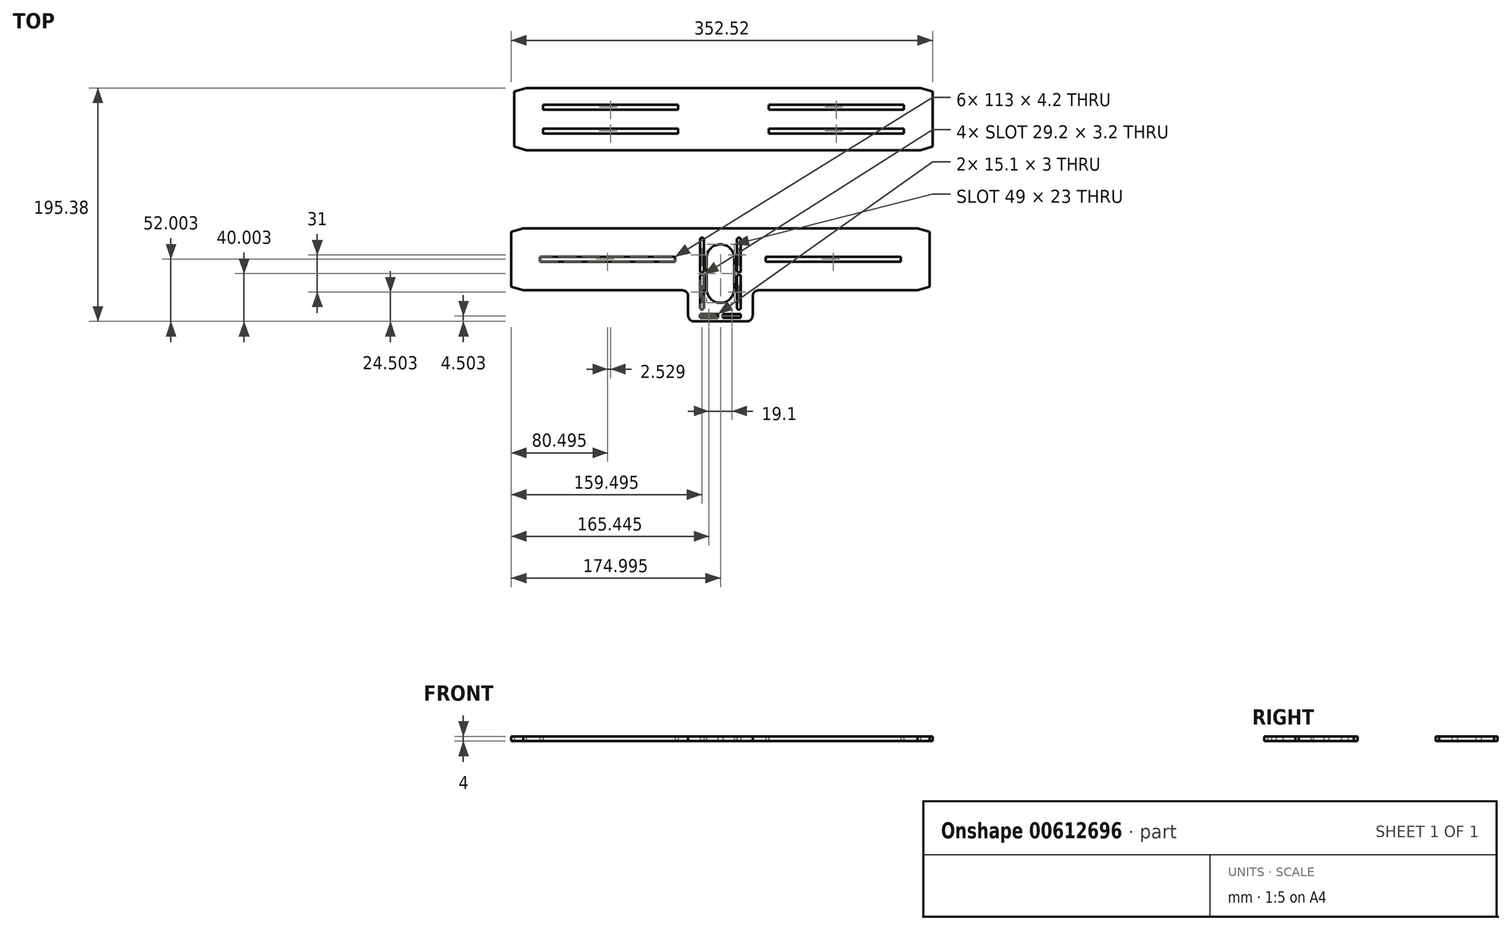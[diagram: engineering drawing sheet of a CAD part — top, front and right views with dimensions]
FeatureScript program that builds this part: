
annotation { "Feature Type Name" : "Feature", "Feature Type Description" : "" }
export const myFeature = defineFeature(function(context is Context, id is Id, definition is map)
    precondition{}
    {
        {
            var Q0;
            Q0=qCreatedBy(makeId("Top.planeOp"),FACE);
            var sketch = newSketch(context, id + "F0", { "sketchPlane" : qUnion([Q0])});
            skLineSegment(sketch, "E0", {"start": v(-166.26, -19.69) * mm, "end": v(-176.26, -22.69) * mm});
            skLineSegment(sketch, "E1", {"start": v(-176.26, -22.69) * mm, "end": v(-176.26, -68.69) * mm});
            skLineSegment(sketch, "E2", {"start": v(-176.26, -68.69) * mm, "end": v(-166.26, -71.69) * mm});
            skLineSegment(sketch, "E3", {"start": v(-166.26, -71.69) * mm, "end": v(-33.26, -71.69) * mm});
            skArc(sketch, "E4", {"start": v(-33.26, -71.69) * mm, "mid": v(-29.73, -73.15) * mm, "end": v(-28.26, -76.69) * mm});
            skLineSegment(sketch, "E5", {"start": v(-28.26, -76.69) * mm, "end": v(-28.26, -92.69) * mm});
            skArc(sketch, "E6", {"start": v(-28.26, -92.69) * mm, "mid": v(-26.8, -96.22) * mm, "end": v(-23.26, -97.69) * mm});
            skLineSegment(sketch, "E7", {"start": v(-23.26, -97.69) * mm, "end": v(20.74, -97.69) * mm});
            skArc(sketch, "E8", {"start": v(20.74, -97.69) * mm, "mid": v(24.27, -96.22) * mm, "end": v(25.74, -92.69) * mm});
            skLineSegment(sketch, "E9", {"start": v(25.74, -92.69) * mm, "end": v(25.74, -76.69) * mm});
            skArc(sketch, "E10", {"start": v(25.74, -76.69) * mm, "mid": v(27.2, -73.15) * mm, "end": v(30.74, -71.69) * mm});
            skLineSegment(sketch, "E11", {"start": v(30.74, -71.69) * mm, "end": v(163.74, -71.69) * mm});
            skLineSegment(sketch, "E12", {"start": v(163.74, -71.69) * mm, "end": v(173.74, -68.69) * mm});
            skLineSegment(sketch, "E13", {"start": v(173.74, -68.69) * mm, "end": v(173.74, -22.69) * mm});
            skLineSegment(sketch, "E14", {"start": v(173.74, -22.69) * mm, "end": v(163.74, -19.69) * mm});
            skLineSegment(sketch, "E15", {"start": v(-173.74, 94.69) * mm, "end": v(-163.74, 97.69) * mm});
            skLineSegment(sketch, "E16", {"start": v(-163.74, 97.69) * mm, "end": v(166.26, 97.69) * mm});
            skLineSegment(sketch, "E17", {"start": v(166.26, 97.69) * mm, "end": v(176.26, 94.69) * mm});
            skLineSegment(sketch, "E18", {"start": v(176.26, 94.69) * mm, "end": v(176.26, 48.69) * mm});
            skLineSegment(sketch, "E19", {"start": v(176.26, 48.69) * mm, "end": v(166.26, 45.69) * mm});
            skLineSegment(sketch, "E20", {"start": v(166.26, 45.69) * mm, "end": v(-163.74, 45.69) * mm});
            skLineSegment(sketch, "E21", {"start": v(-163.74, 45.69) * mm, "end": v(-173.74, 48.69) * mm});
            skLineSegment(sketch, "E22", {"start": v(-173.74, 48.69) * mm, "end": v(-173.74, 94.69) * mm});
            skLineSegment(sketch, "E23", {"start": v(-18.36, -29.19) * mm, "end": v(-18.36, -55.19) * mm});
            skArc(sketch, "E24", {"start": v(-18.36, -55.19) * mm, "mid": v(-16.76, -56.79) * mm, "end": v(-15.16, -55.19) * mm});
            skLineSegment(sketch, "E25", {"start": v(-15.16, -55.19) * mm, "end": v(-15.16, -29.19) * mm});
            skArc(sketch, "E26", {"start": v(-15.16, -29.19) * mm, "mid": v(-16.76, -27.59) * mm, "end": v(-18.36, -29.19) * mm});
            skLineSegment(sketch, "E27", {"start": v(12.64, -29.19) * mm, "end": v(12.64, -55.19) * mm});
            skArc(sketch, "E28", {"start": v(12.64, -55.19) * mm, "mid": v(14.24, -56.79) * mm, "end": v(15.84, -55.19) * mm});
            skLineSegment(sketch, "E29", {"start": v(15.84, -55.19) * mm, "end": v(15.84, -29.19) * mm});
            skArc(sketch, "E30", {"start": v(15.84, -29.19) * mm, "mid": v(14.24, -27.59) * mm, "end": v(12.64, -29.19) * mm});
            skLineSegment(sketch, "E31", {"start": v(-15.16, -86.19) * mm, "end": v(-15.16, -60.19) * mm});
            skArc(sketch, "E32", {"start": v(-15.16, -60.19) * mm, "mid": v(-16.76, -58.59) * mm, "end": v(-18.36, -60.19) * mm});
            skLineSegment(sketch, "E33", {"start": v(-18.36, -60.19) * mm, "end": v(-18.36, -86.19) * mm});
            skArc(sketch, "E34", {"start": v(-18.36, -86.19) * mm, "mid": v(-16.76, -87.79) * mm, "end": v(-15.16, -86.19) * mm});
            skLineSegment(sketch, "E35", {"start": v(15.84, -86.19) * mm, "end": v(15.84, -60.19) * mm});
            skArc(sketch, "E36", {"start": v(15.84, -60.19) * mm, "mid": v(14.24, -58.59) * mm, "end": v(12.64, -60.19) * mm});
            skLineSegment(sketch, "E37", {"start": v(12.64, -60.19) * mm, "end": v(12.64, -86.19) * mm});
            skArc(sketch, "E38", {"start": v(12.64, -86.19) * mm, "mid": v(14.24, -87.79) * mm, "end": v(15.84, -86.19) * mm});
            skLineSegment(sketch, "E39", {"start": v(-12.76, -44.69) * mm, "end": v(-12.76, -70.69) * mm});
            skArc(sketch, "E40", {"start": v(-12.76, -70.69) * mm, "mid": v(-1.26, -82.19) * mm, "end": v(10.24, -70.69) * mm});
            skLineSegment(sketch, "E41", {"start": v(10.24, -70.69) * mm, "end": v(10.24, -44.69) * mm});
            skArc(sketch, "E42", {"start": v(10.24, -44.69) * mm, "mid": v(-1.26, -33.19) * mm, "end": v(-12.76, -44.69) * mm});
            skLineSegment(sketch, "E43", {"start": v(36.74, -43.59) * mm, "end": v(149.74, -43.59) * mm});
            skLineSegment(sketch, "E44", {"start": v(-152.26, -43.59) * mm, "end": v(-39.26, -43.59) * mm});
            skLineSegment(sketch, "E45", {"start": v(36.74, -47.79) * mm, "end": v(149.74, -47.79) * mm});
            skLineSegment(sketch, "E46", {"start": v(-152.26, -47.79) * mm, "end": v(-39.26, -47.79) * mm});
            skLineSegment(sketch, "E47", {"start": v(-36.74, 59.59) * mm, "end": v(-36.74, 63.79) * mm});
            skLineSegment(sketch, "E48", {"start": v(-36.74, 79.59) * mm, "end": v(-36.74, 83.79) * mm});
            skLineSegment(sketch, "E49", {"start": v(-39.26, -47.79) * mm, "end": v(-39.26, -43.59) * mm});
            skLineSegment(sketch, "E50", {"start": v(39.26, 79.59) * mm, "end": v(39.26, 83.79) * mm});
            skLineSegment(sketch, "E51", {"start": v(39.26, 59.59) * mm, "end": v(39.26, 63.79) * mm});
            skLineSegment(sketch, "E52", {"start": v(36.74, -47.79) * mm, "end": v(36.74, -43.59) * mm});
            skLineSegment(sketch, "E53", {"start": v(-152.26, -47.79) * mm, "end": v(-152.26, -43.59) * mm});
            skLineSegment(sketch, "E54", {"start": v(-149.74, 79.59) * mm, "end": v(-149.74, 83.79) * mm});
            skLineSegment(sketch, "E55", {"start": v(-149.74, 59.59) * mm, "end": v(-149.74, 63.79) * mm});
            skLineSegment(sketch, "E56", {"start": v(152.26, 59.59) * mm, "end": v(152.26, 63.79) * mm});
            skLineSegment(sketch, "E57", {"start": v(152.26, 79.59) * mm, "end": v(152.26, 83.79) * mm});
            skLineSegment(sketch, "E58", {"start": v(149.74, -47.79) * mm, "end": v(149.74, -43.59) * mm});
            skLineSegment(sketch, "E59", {"start": v(39.26, 83.79) * mm, "end": v(152.26, 83.79) * mm});
            skLineSegment(sketch, "E60", {"start": v(-149.74, 83.79) * mm, "end": v(-36.74, 83.79) * mm});
            skLineSegment(sketch, "E61", {"start": v(39.26, 79.59) * mm, "end": v(152.26, 79.59) * mm});
            skLineSegment(sketch, "E62", {"start": v(-149.74, 79.59) * mm, "end": v(-36.74, 79.59) * mm});
            skLineSegment(sketch, "E63", {"start": v(39.26, 63.79) * mm, "end": v(152.26, 63.79) * mm});
            skLineSegment(sketch, "E64", {"start": v(-149.74, 63.79) * mm, "end": v(-36.74, 63.79) * mm});
            skLineSegment(sketch, "E65", {"start": v(39.26, 59.59) * mm, "end": v(152.26, 59.59) * mm});
            skLineSegment(sketch, "E66", {"start": v(-149.74, 59.59) * mm, "end": v(-36.74, 59.59) * mm});
            skLineSegment(sketch, "E67", {"start": v(0.74, -94.69) * mm, "end": v(15.84, -94.69) * mm});
            skLineSegment(sketch, "E68", {"start": v(-18.36, -94.69) * mm, "end": v(-3.26, -94.69) * mm});
            skLineSegment(sketch, "E69", {"start": v(0.74, -91.69) * mm, "end": v(15.84, -91.69) * mm});
            skLineSegment(sketch, "E70", {"start": v(-18.36, -91.69) * mm, "end": v(-3.26, -91.69) * mm});
            skLineSegment(sketch, "E71", {"start": v(-18.36, -91.69) * mm, "end": v(-18.36, -94.69) * mm});
            skLineSegment(sketch, "E72", {"start": v(15.84, -91.69) * mm, "end": v(15.84, -94.69) * mm});
            skLineSegment(sketch, "E73", {"start": v(-3.26, -91.69) * mm, "end": v(-3.26, -94.69) * mm});
            skLineSegment(sketch, "E74", {"start": v(0.74, -91.69) * mm, "end": v(0.74, -94.69) * mm});
            skLineSegment(sketch, "E75", {"start": v(-166.26, -19.69) * mm, "end": v(163.74, -19.69) * mm});
            skSolve(sketch);
        }
        {
            var Q0;
            Q0=makeQuery(id+"F0.imprint","IMPRINT",FACE,{"disambiguationData":[TD([[makeQuery(id+"F0.imprint","IMPRINT",EDGE,{"derivedFrom":sQuery(id+"F0.wireOp",EDGE,"E15")}),-1.0]])]});
            var Q1;
            Q1=makeQuery(id+"F0.imprint","IMPRINT",FACE,{"disambiguationData":[TD([[makeQuery(id+"F0.imprint","IMPRINT",EDGE,{"derivedFrom":sQuery(id+"F0.wireOp",EDGE,"E0")}),1.0]])]});
            extrude(context, id + "F1", {"entities" : qUnion([Q0, Q1]), "depth" : 4 * mm, "offsetDistance" : 25 * mm});
        }
    });
